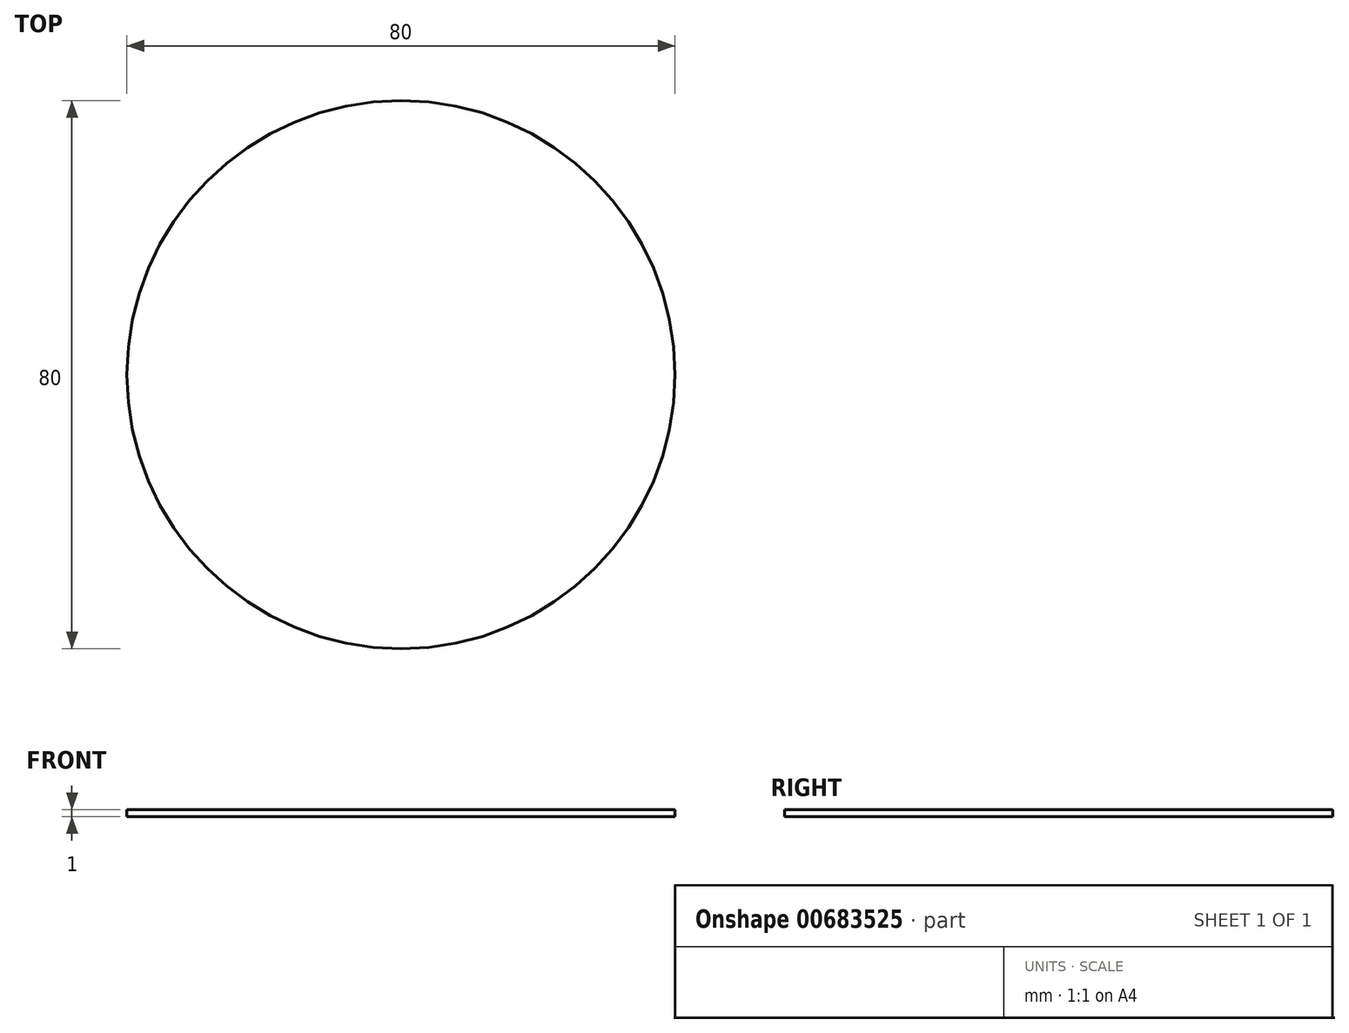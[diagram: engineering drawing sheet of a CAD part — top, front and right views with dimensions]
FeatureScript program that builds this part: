
annotation { "Feature Type Name" : "Feature", "Feature Type Description" : "" }
export const myFeature = defineFeature(function(context is Context, id is Id, definition is map)
    precondition{}
    {
        {
            var Q0;
            Q0=qCreatedBy(makeId("Top.planeOp"),FACE);
            var sketch = newSketch(context, id + "F0", { "sketchPlane" : qUnion([Q0])});
            skCircle(sketch, "E0", {"center": v(0, 0) * mm, "radius": 40 * mm});
            skSolve(sketch);
        }
        {
            var Q0;
            Q0 = qSketchRegion(id + "F0", true);
            extrude(context, id + "F1", {"entities" : qUnion([Q0]), "depth" : 1 * mm, "offsetDistance" : 25 * mm});
        }
    });
